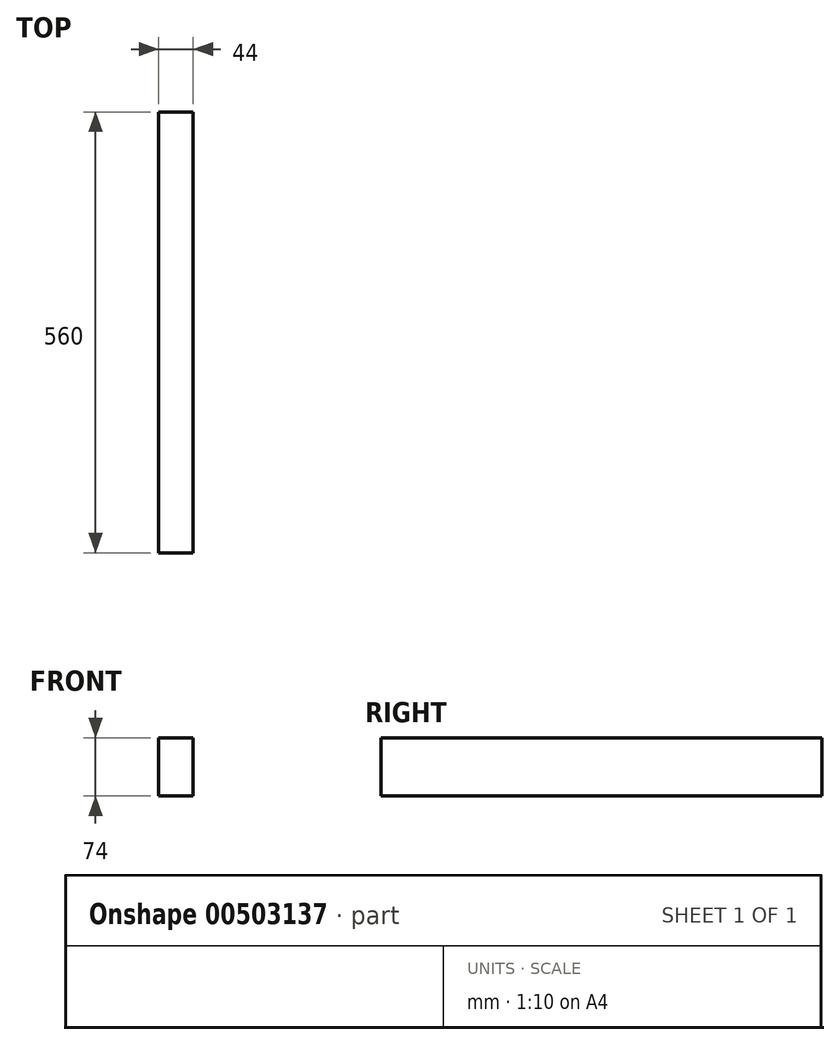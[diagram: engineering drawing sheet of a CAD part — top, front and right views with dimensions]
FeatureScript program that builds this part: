
annotation { "Feature Type Name" : "Feature", "Feature Type Description" : "" }
export const myFeature = defineFeature(function(context is Context, id is Id, definition is map)
    precondition{}
    {
        {
            var Q0;
            Q0=qCreatedBy(makeId("Right.planeOp"),FACE);
            var sketch = newSketch(context, id + "F0", { "sketchPlane" : qUnion([Q0])});
            skLineSegment(sketch, "E0.bottom", {"start": v(300, 45) * mm, "end": v(-260, 45) * mm});
            skLineSegment(sketch, "E0.top", {"start": v(300, -29) * mm, "end": v(-260, -29) * mm});
            skLineSegment(sketch, "E0.left", {"start": v(300, 45) * mm, "end": v(300, -29) * mm});
            skLineSegment(sketch, "E0.right", {"start": v(-260, 45) * mm, "end": v(-260, -29) * mm});
            skSolve(sketch);
        }
        {
            var Q0;
            Q0=makeQuery(id+"F0.imprint","IMPRINT",FACE,{"disambiguationData":[TD([[makeQuery(id+"F0.imprint","IMPRINT",EDGE,{"derivedFrom":sQuery(id+"F0.wireOp",EDGE,"E0.bottom")}),1.0]])]});
            extrude(context, id + "F1", {"entities" : qUnion([Q0]), "depth" : 44 * mm, "offsetDistance" : 25 * mm});
        }
    });
